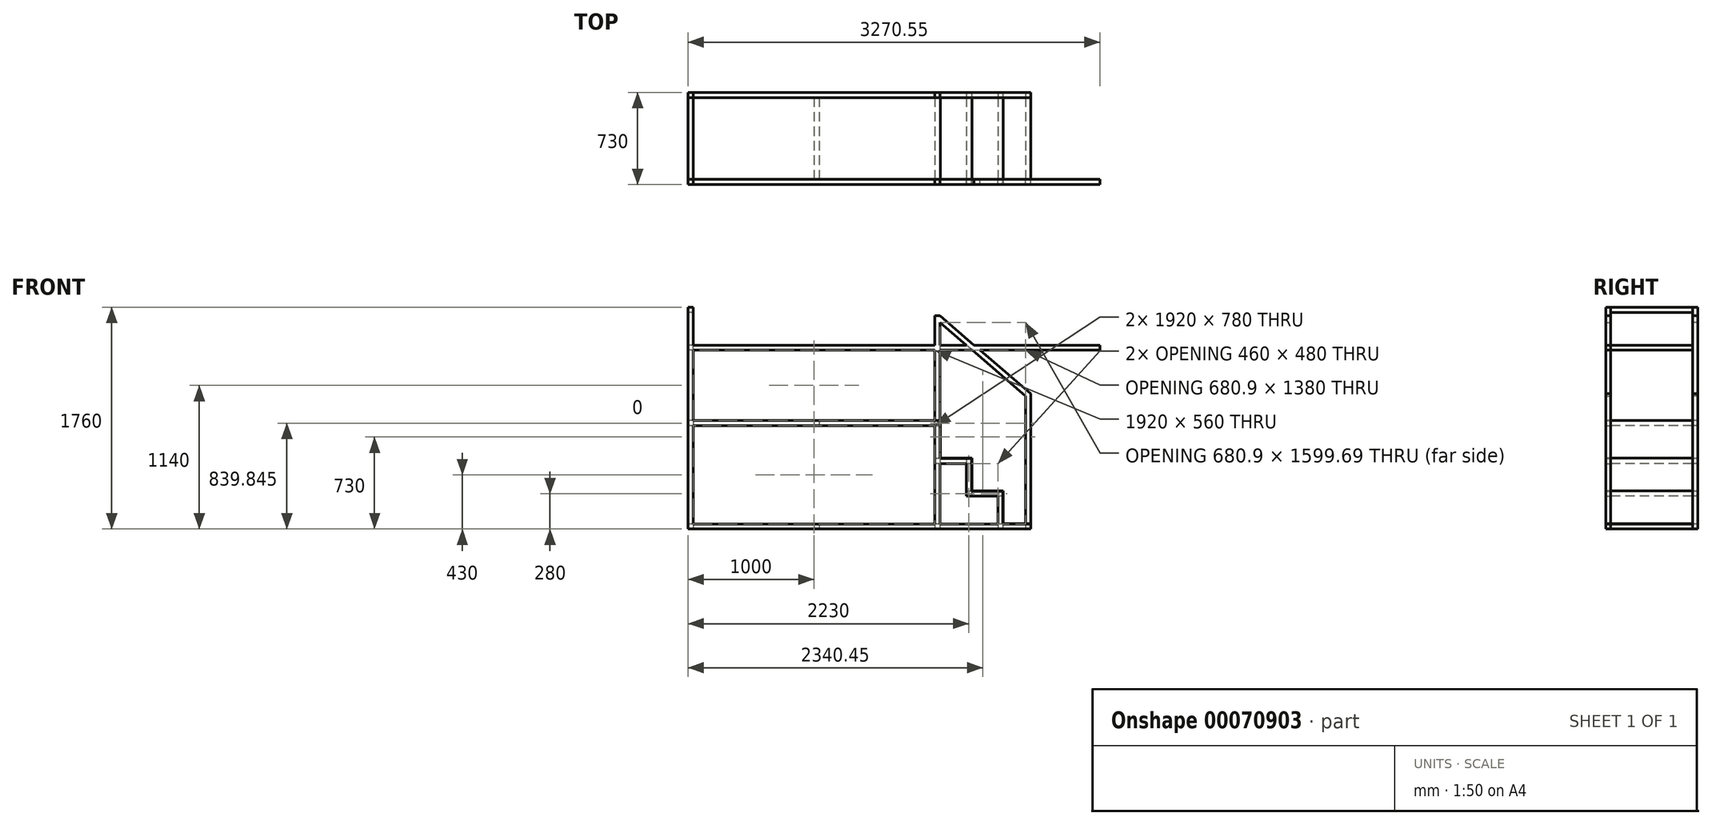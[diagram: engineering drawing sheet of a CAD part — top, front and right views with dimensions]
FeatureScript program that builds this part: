
annotation { "Feature Type Name" : "Feature", "Feature Type Description" : "" }
export const myFeature = defineFeature(function(context is Context, id is Id, definition is map)
    precondition{}
    {
        {
            var Q0;
            Q0=qCreatedBy(makeId("Front.planeOp"),FACE);
            var sketch = newSketch(context, id + "F0", { "sketchPlane" : qUnion([Q0])});
            skLineSegment(sketch, "E0", {"start": v(40, 0) * mm, "end": v(1960, 0) * mm});
            skLineSegment(sketch, "E1.0", {"start": v(40, 40) * mm, "end": v(1960, 40) * mm});
            skLineSegment(sketch, "E2", {"start": v(0, 40) * mm, "end": v(0, 0) * mm});
            skLineSegment(sketch, "E3.0", {"start": v(2000, 40) * mm, "end": v(2000, 0) * mm});
            skLineSegment(sketch, "E4", {"start": v(0, 0) * mm, "end": v(0, -820) * mm});
            skLineSegment(sketch, "E5", {"start": v(2000, 0) * mm, "end": v(2000, -260) * mm});
            skLineSegment(sketch, "E6", {"start": v(0, -820) * mm, "end": v(2000, -820) * mm});
            skLineSegment(sketch, "E7.0", {"start": v(40, -780) * mm, "end": v(1960, -780) * mm});
            skLineSegment(sketch, "E8.0", {"start": v(40, 0) * mm, "end": v(40, -780) * mm});
            skLineSegment(sketch, "E9.0", {"start": v(1960, 0) * mm, "end": v(1960, -780) * mm});
            skLineSegment(sketch, "E10", {"start": v(0, 40) * mm, "end": v(0, 940) * mm});
            skLineSegment(sketch, "E11", {"start": v(0, 940) * mm, "end": v(2000, 940) * mm});
            skLineSegment(sketch, "E12", {"start": v(2000, 940) * mm, "end": v(2000, 872.37) * mm});
            skLineSegment(sketch, "E13", {"start": v(40, 40) * mm, "end": v(40, 900) * mm});
            skLineSegment(sketch, "E14", {"start": v(40, 900) * mm, "end": v(1960, 900) * mm});
            skLineSegment(sketch, "E15", {"start": v(1960, 900) * mm, "end": v(1960, 40) * mm});
            skLineSegment(sketch, "E16", {"start": v(2000, 872.37) * mm, "end": v(2720.9, 254.57) * mm});
            skLineSegment(sketch, "E17", {"start": v(2720.9, 254.57) * mm, "end": v(2720.9, -820) * mm});
            skLineSegment(sketch, "E18", {"start": v(2720.9, -820) * mm, "end": v(2000, -820) * mm});
            skLineSegment(sketch, "E19", {"start": v(1960, -780) * mm, "end": v(2460, -780) * mm});
            skLineSegment(sketch, "E20", {"start": v(2680.9, -780) * mm, "end": v(2680.9, 236.17) * mm});
            skLineSegment(sketch, "E21", {"start": v(2680.9, 236.17) * mm, "end": v(2000, 819.7) * mm});
            skLineSegment(sketch, "E22", {"start": v(2000, -300) * mm, "end": v(2210, -300) * mm});
            skLineSegment(sketch, "E23", {"start": v(2210, -300) * mm, "end": v(2210, -560) * mm});
            skLineSegment(sketch, "E24", {"start": v(2210, -560) * mm, "end": v(2460, -560) * mm});
            skLineSegment(sketch, "E25", {"start": v(2460, -560) * mm, "end": v(2460, -780) * mm});
            skLineSegment(sketch, "E26", {"start": v(2000, -260) * mm, "end": v(2250, -260) * mm});
            skLineSegment(sketch, "E27", {"start": v(2250, -260) * mm, "end": v(2250, -520) * mm});
            skLineSegment(sketch, "E28", {"start": v(2250, -520) * mm, "end": v(2500, -520) * mm});
            skLineSegment(sketch, "E29", {"start": v(2500, -520) * mm, "end": v(2500, -780) * mm});
            skLineSegment(sketch, "E30.trimOffspring", {"start": v(2000, -300) * mm, "end": v(2000, -820) * mm});
            skLineSegment(sketch, "E31.trimOffspring", {"start": v(2500, -780) * mm, "end": v(2680.9, -780) * mm});
            skLineSegment(sketch, "E32.trimOffspring", {"start": v(2000, 819.7) * mm, "end": v(2000, 40) * mm});
            skSolve(sketch);
        }
        {
            var Q0;
            Q0=makeQuery(id+"F0.imprint","IMPRINT",FACE,{"disambiguationData":[TD([[makeQuery(id+"F0.imprint","IMPRINT",EDGE,{"derivedFrom":sQuery(id+"F0.wireOp",EDGE,"E0")}),1.0]])]});
            extrude(context, id + "F1", {"entities" : qUnion([Q0]), "depth" : 40 * mm});
        }
        {
            var Q0;
            Q0=makeQuery(id+"F1.opExtrude","CAP_FACE",FACE,{"disambiguationData":[OSD([sQuery(id+"F0.wireOp",EDGE,"E0"),sQuery(id+"F0.wireOp",EDGE,"E1.0"),sQuery(id+"F0.wireOp",EDGE,"E2"),sQuery(id+"F0.wireOp",EDGE,"E3.0"),sQuery(id+"F0.wireOp",EDGE,"E4"),sQuery(id+"F0.wireOp",EDGE,"E5"),sQuery(id+"F0.wireOp",EDGE,"E6"),sQuery(id+"F0.wireOp",EDGE,"E7.0"),sQuery(id+"F0.wireOp",EDGE,"E8.0"),sQuery(id+"F0.wireOp",EDGE,"E9.0"),sQuery(id+"F0.wireOp",EDGE,"E10"),sQuery(id+"F0.wireOp",EDGE,"E11"),sQuery(id+"F0.wireOp",EDGE,"E12"),sQuery(id+"F0.wireOp",EDGE,"E13"),sQuery(id+"F0.wireOp",EDGE,"E14"),sQuery(id+"F0.wireOp",EDGE,"E15"),sQuery(id+"F0.wireOp",EDGE,"E16"),sQuery(id+"F0.wireOp",EDGE,"E17"),sQuery(id+"F0.wireOp",EDGE,"E18"),sQuery(id+"F0.wireOp",EDGE,"E19"),sQuery(id+"F0.wireOp",EDGE,"E20"),sQuery(id+"F0.wireOp",EDGE,"E21"),sQuery(id+"F0.wireOp",EDGE,"E22"),sQuery(id+"F0.wireOp",EDGE,"E23"),sQuery(id+"F0.wireOp",EDGE,"E24"),sQuery(id+"F0.wireOp",EDGE,"E25"),sQuery(id+"F0.wireOp",EDGE,"E26"),sQuery(id+"F0.wireOp",EDGE,"E27"),sQuery(id+"F0.wireOp",EDGE,"E28"),sQuery(id+"F0.wireOp",EDGE,"E29"),sQuery(id+"F0.wireOp",EDGE,"E30.trimOffspring"),sQuery(id+"F0.wireOp",EDGE,"E31.trimOffspring"),sQuery(id+"F0.wireOp",EDGE,"E32.trimOffspring")])],"isStart":true});
            var sketch = newSketch(context, id + "F2", { "sketchPlane" : qUnion([Q0])});
            skLineSegment(sketch, "E33.bottom", {"start": v(-1960, 0) * mm, "end": v(-2000, 0) * mm});
            skLineSegment(sketch, "E33.top", {"start": v(-1960, 40) * mm, "end": v(-2000, 40) * mm});
            skLineSegment(sketch, "E33.left", {"start": v(-1960, 0) * mm, "end": v(-1960, 40) * mm});
            skLineSegment(sketch, "E33.right", {"start": v(-2000, 0) * mm, "end": v(-2000, 40) * mm});
            skLineSegment(sketch, "E34.bottom", {"start": v(-2000, -260) * mm, "end": v(-1960, -260) * mm});
            skLineSegment(sketch, "E34.top", {"start": v(-2000, -300) * mm, "end": v(-1960, -300) * mm});
            skLineSegment(sketch, "E34.left", {"start": v(-2000, -260) * mm, "end": v(-2000, -300) * mm});
            skLineSegment(sketch, "E34.right", {"start": v(-1960, -260) * mm, "end": v(-1960, -300) * mm});
            skLineSegment(sketch, "E35.bottom", {"start": v(-2250, -260) * mm, "end": v(-2210, -260) * mm});
            skLineSegment(sketch, "E35.top", {"start": v(-2250, -300) * mm, "end": v(-2210, -300) * mm});
            skLineSegment(sketch, "E35.left", {"start": v(-2250, -260) * mm, "end": v(-2250, -300) * mm});
            skLineSegment(sketch, "E35.right", {"start": v(-2210, -260) * mm, "end": v(-2210, -300) * mm});
            skLineSegment(sketch, "E36.bottom", {"start": v(-2250, -520) * mm, "end": v(-2210, -520) * mm});
            skLineSegment(sketch, "E36.top", {"start": v(-2250, -560) * mm, "end": v(-2210, -560) * mm});
            skLineSegment(sketch, "E36.left", {"start": v(-2250, -520) * mm, "end": v(-2250, -560) * mm});
            skLineSegment(sketch, "E36.right", {"start": v(-2210, -520) * mm, "end": v(-2210, -560) * mm});
            skLineSegment(sketch, "E37.bottom", {"start": v(-2500, -520) * mm, "end": v(-2460, -520) * mm});
            skLineSegment(sketch, "E37.top", {"start": v(-2500, -560) * mm, "end": v(-2460, -560) * mm});
            skLineSegment(sketch, "E37.left", {"start": v(-2500, -520) * mm, "end": v(-2500, -560) * mm});
            skLineSegment(sketch, "E37.right", {"start": v(-2460, -520) * mm, "end": v(-2460, -560) * mm});
            skLineSegment(sketch, "E38.bottom", {"start": v(-2680.9, -780) * mm, "end": v(-2720.9, -780) * mm});
            skLineSegment(sketch, "E38.top", {"start": v(-2680.9, -820) * mm, "end": v(-2720.9, -820) * mm});
            skLineSegment(sketch, "E38.left", {"start": v(-2680.9, -780) * mm, "end": v(-2680.9, -820) * mm});
            skLineSegment(sketch, "E38.right", {"start": v(-2720.9, -780) * mm, "end": v(-2720.9, -820) * mm});
            skLineSegment(sketch, "E39.bottom", {"start": v(-40, 40) * mm, "end": v(0, 40) * mm});
            skLineSegment(sketch, "E39.top", {"start": v(-40, 0) * mm, "end": v(0, 0) * mm});
            skLineSegment(sketch, "E39.left", {"start": v(-40, 40) * mm, "end": v(-40, 0) * mm});
            skLineSegment(sketch, "E39.right", {"start": v(0, 40) * mm, "end": v(0, 0) * mm});
            skLineSegment(sketch, "E40.bottom", {"start": v(-40, -780) * mm, "end": v(0, -780) * mm});
            skLineSegment(sketch, "E40.top", {"start": v(-40, -820) * mm, "end": v(0, -820) * mm});
            skLineSegment(sketch, "E40.left", {"start": v(-40, -780) * mm, "end": v(-40, -820) * mm});
            skLineSegment(sketch, "E40.right", {"start": v(0, -780) * mm, "end": v(0, -820) * mm});
            skLineSegment(sketch, "E41.bottom", {"start": v(-2500, -780) * mm, "end": v(-2460, -780) * mm});
            skLineSegment(sketch, "E41.top", {"start": v(-2500, -820) * mm, "end": v(-2460, -820) * mm});
            skLineSegment(sketch, "E41.left", {"start": v(-2500, -780) * mm, "end": v(-2500, -820) * mm});
            skLineSegment(sketch, "E41.right", {"start": v(-2460, -780) * mm, "end": v(-2460, -820) * mm});
            skLineSegment(sketch, "E42.bottom", {"start": v(-2000, -780) * mm, "end": v(-1960, -780) * mm});
            skLineSegment(sketch, "E42.top", {"start": v(-2000, -820) * mm, "end": v(-1960, -820) * mm});
            skLineSegment(sketch, "E42.left", {"start": v(-2000, -780) * mm, "end": v(-2000, -820) * mm});
            skLineSegment(sketch, "E42.right", {"start": v(-1960, -780) * mm, "end": v(-1960, -820) * mm});
            skLineSegment(sketch, "E43.bottom", {"start": v(-1040, 40) * mm, "end": v(-1000, 40) * mm});
            skLineSegment(sketch, "E43.top", {"start": v(-1040, 0) * mm, "end": v(-1000, 0) * mm});
            skLineSegment(sketch, "E43.left", {"start": v(-1040, 40) * mm, "end": v(-1040, 0) * mm});
            skLineSegment(sketch, "E43.right", {"start": v(-1000, 40) * mm, "end": v(-1000, 0) * mm});
            skLineSegment(sketch, "E44.bottom", {"start": v(-1040, -780) * mm, "end": v(-1000, -780) * mm});
            skLineSegment(sketch, "E44.top", {"start": v(-1040, -820) * mm, "end": v(-1000, -820) * mm});
            skLineSegment(sketch, "E44.left", {"start": v(-1040, -780) * mm, "end": v(-1040, -820) * mm});
            skLineSegment(sketch, "E44.right", {"start": v(-1000, -780) * mm, "end": v(-1000, -820) * mm});
            skLineSegment(sketch, "E45.bottom", {"start": v(-40, 900) * mm, "end": v(0, 900) * mm});
            skLineSegment(sketch, "E45.top", {"start": v(-40, 940) * mm, "end": v(0, 940) * mm});
            skLineSegment(sketch, "E45.left", {"start": v(-40, 900) * mm, "end": v(-40, 940) * mm});
            skLineSegment(sketch, "E45.right", {"start": v(0, 900) * mm, "end": v(0, 940) * mm});
            skSolve(sketch);
        }
        {
            var Q0;
            Q0=makeQuery(id+"F2.imprint","IMPRINT",FACE,{"disambiguationData":[TD([[makeQuery(id+"F2.imprint","IMPRINT",EDGE,{"derivedFrom":sQuery(id+"F2.wireOp",EDGE,"E45.bottom")}),1.0]])]});
            var Q1;
            Q1=makeQuery(id+"F2.imprint","IMPRINT",FACE,{"disambiguationData":[TD([[makeQuery(id+"F2.imprint","IMPRINT",EDGE,{"derivedFrom":sQuery(id+"F2.wireOp",EDGE,"E39.bottom")}),-1.0]])]});
            var Q2;
            Q2=makeQuery(id+"F2.imprint","IMPRINT",FACE,{"disambiguationData":[TD([[makeQuery(id+"F2.imprint","IMPRINT",EDGE,{"derivedFrom":sQuery(id+"F2.wireOp",EDGE,"E40.bottom")}),-1.0]])]});
            var Q3;
            Q3=makeQuery(id+"F2.imprint","IMPRINT",FACE,{"disambiguationData":[TD([[makeQuery(id+"F2.imprint","IMPRINT",EDGE,{"derivedFrom":sQuery(id+"F2.wireOp",EDGE,"E44.bottom")}),1.0]])]});
            var Q4;
            Q4=makeQuery(id+"F2.imprint","IMPRINT",FACE,{"disambiguationData":[TD([[makeQuery(id+"F2.imprint","IMPRINT",EDGE,{"derivedFrom":sQuery(id+"F2.wireOp",EDGE,"E43.bottom")}),1.0]])]});
            var Q5;
            Q5=makeQuery(id+"F2.imprint","IMPRINT",FACE,{"disambiguationData":[TD([[makeQuery(id+"F2.imprint","IMPRINT",EDGE,{"derivedFrom":sQuery(id+"F2.wireOp",EDGE,"E33.bottom")}),-1.0]])]});
            var Q6;
            Q6=makeQuery(id+"F2.imprint","IMPRINT",FACE,{"disambiguationData":[TD([[makeQuery(id+"F2.imprint","IMPRINT",EDGE,{"derivedFrom":sQuery(id+"F2.wireOp",EDGE,"E42.bottom")}),-1.0]])]});
            var Q7;
            Q7=makeQuery(id+"F2.imprint","IMPRINT",FACE,{"disambiguationData":[TD([[makeQuery(id+"F2.imprint","IMPRINT",EDGE,{"derivedFrom":sQuery(id+"F2.wireOp",EDGE,"E34.bottom")}),-1.0]])]});
            var Q8;
            Q8=makeQuery(id+"F2.imprint","IMPRINT",FACE,{"disambiguationData":[TD([[makeQuery(id+"F2.imprint","IMPRINT",EDGE,{"derivedFrom":sQuery(id+"F2.wireOp",EDGE,"E35.bottom")}),1.0]])]});
            var Q9;
            Q9=makeQuery(id+"F2.imprint","IMPRINT",FACE,{"disambiguationData":[TD([[makeQuery(id+"F2.imprint","IMPRINT",EDGE,{"derivedFrom":sQuery(id+"F2.wireOp",EDGE,"E37.bottom")}),1.0]])]});
            var Q10;
            Q10=makeQuery(id+"F2.imprint","IMPRINT",FACE,{"disambiguationData":[TD([[makeQuery(id+"F2.imprint","IMPRINT",EDGE,{"derivedFrom":sQuery(id+"F2.wireOp",EDGE,"E36.bottom")}),-1.0]])]});
            var Q11;
            Q11=makeQuery(id+"F2.imprint","IMPRINT",FACE,{"disambiguationData":[TD([[makeQuery(id+"F2.imprint","IMPRINT",EDGE,{"derivedFrom":sQuery(id+"F2.wireOp",EDGE,"E41.bottom")}),-1.0]])]});
            var Q12;
            Q12=makeQuery(id+"F2.imprint","IMPRINT",FACE,{"disambiguationData":[TD([[makeQuery(id+"F2.imprint","IMPRINT",EDGE,{"derivedFrom":sQuery(id+"F2.wireOp",EDGE,"E38.bottom")}),1.0]])]});
            extrude(context, id + "F3", {"entities" : qUnion([Q0, Q1, Q2, Q3, Q4, Q5, Q6, Q7, Q8, Q9, Q10, Q11, Q12]), "depth" : 650 * mm});
        }
        {
            var Q0;
            Q0=makeQuery(id+"F1.opExtrude","CAP_FACE",FACE,{"disambiguationData":[OSD([sQuery(id+"F0.wireOp",EDGE,"E0"),sQuery(id+"F0.wireOp",EDGE,"E1.0"),sQuery(id+"F0.wireOp",EDGE,"E2"),sQuery(id+"F0.wireOp",EDGE,"E3.0"),sQuery(id+"F0.wireOp",EDGE,"E4"),sQuery(id+"F0.wireOp",EDGE,"E5"),sQuery(id+"F0.wireOp",EDGE,"E6"),sQuery(id+"F0.wireOp",EDGE,"E7.0"),sQuery(id+"F0.wireOp",EDGE,"E8.0"),sQuery(id+"F0.wireOp",EDGE,"E9.0"),sQuery(id+"F0.wireOp",EDGE,"E10"),sQuery(id+"F0.wireOp",EDGE,"E11"),sQuery(id+"F0.wireOp",EDGE,"E12"),sQuery(id+"F0.wireOp",EDGE,"E13"),sQuery(id+"F0.wireOp",EDGE,"E14"),sQuery(id+"F0.wireOp",EDGE,"E15"),sQuery(id+"F0.wireOp",EDGE,"E16"),sQuery(id+"F0.wireOp",EDGE,"E17"),sQuery(id+"F0.wireOp",EDGE,"E18"),sQuery(id+"F0.wireOp",EDGE,"E19"),sQuery(id+"F0.wireOp",EDGE,"E20"),sQuery(id+"F0.wireOp",EDGE,"E21"),sQuery(id+"F0.wireOp",EDGE,"E22"),sQuery(id+"F0.wireOp",EDGE,"E23"),sQuery(id+"F0.wireOp",EDGE,"E24"),sQuery(id+"F0.wireOp",EDGE,"E25"),sQuery(id+"F0.wireOp",EDGE,"E26"),sQuery(id+"F0.wireOp",EDGE,"E27"),sQuery(id+"F0.wireOp",EDGE,"E28"),sQuery(id+"F0.wireOp",EDGE,"E29"),sQuery(id+"F0.wireOp",EDGE,"E30.trimOffspring"),sQuery(id+"F0.wireOp",EDGE,"E31.trimOffspring"),sQuery(id+"F0.wireOp",EDGE,"E32.trimOffspring")])],"isStart":true});
            cPlane(context, id + "F4", {"entities" : qUnion([Q0]), "cplaneType" : CPlaneType.OFFSET, "offset" : 325 * mm, "width" : 150 * mm, "height" : 150 * mm});
        }
        {
            var Q0;
            Q0=makeQuery(id+"F1.opExtrude","SWEPT_BODY",BODY,{"disambiguationData":[OSD([sQuery(id+"F0.wireOp",EDGE,"E0"),sQuery(id+"F0.wireOp",EDGE,"E1.0"),sQuery(id+"F0.wireOp",EDGE,"E2"),sQuery(id+"F0.wireOp",EDGE,"E3.0"),sQuery(id+"F0.wireOp",EDGE,"E4"),sQuery(id+"F0.wireOp",EDGE,"E5"),sQuery(id+"F0.wireOp",EDGE,"E6"),sQuery(id+"F0.wireOp",EDGE,"E7.0"),sQuery(id+"F0.wireOp",EDGE,"E8.0"),sQuery(id+"F0.wireOp",EDGE,"E9.0"),sQuery(id+"F0.wireOp",EDGE,"E10"),sQuery(id+"F0.wireOp",EDGE,"E11"),sQuery(id+"F0.wireOp",EDGE,"E12"),sQuery(id+"F0.wireOp",EDGE,"E13"),sQuery(id+"F0.wireOp",EDGE,"E14"),sQuery(id+"F0.wireOp",EDGE,"E15"),sQuery(id+"F0.wireOp",EDGE,"E16"),sQuery(id+"F0.wireOp",EDGE,"E17"),sQuery(id+"F0.wireOp",EDGE,"E18"),sQuery(id+"F0.wireOp",EDGE,"E19"),sQuery(id+"F0.wireOp",EDGE,"E20"),sQuery(id+"F0.wireOp",EDGE,"E21"),sQuery(id+"F0.wireOp",EDGE,"E22"),sQuery(id+"F0.wireOp",EDGE,"E23"),sQuery(id+"F0.wireOp",EDGE,"E24"),sQuery(id+"F0.wireOp",EDGE,"E25"),sQuery(id+"F0.wireOp",EDGE,"E26"),sQuery(id+"F0.wireOp",EDGE,"E27"),sQuery(id+"F0.wireOp",EDGE,"E28"),sQuery(id+"F0.wireOp",EDGE,"E29"),sQuery(id+"F0.wireOp",EDGE,"E30.trimOffspring"),sQuery(id+"F0.wireOp",EDGE,"E31.trimOffspring"),sQuery(id+"F0.wireOp",EDGE,"E32.trimOffspring")])]});
            var Q1;
            Q1=qCreatedBy(id+"F4.planeOp",FACE);
            mirror(context, id + "F5", {"entities" : qUnion([Q0]), "mirrorPlane" : qUnion([Q1])});
        }
        {
            var Q0;
            Q0=makeQuery(id+"F1.opExtrude","CAP_FACE",FACE,{"disambiguationData":[OSD([sQuery(id+"F0.wireOp",EDGE,"E0"),sQuery(id+"F0.wireOp",EDGE,"E1.0"),sQuery(id+"F0.wireOp",EDGE,"E2"),sQuery(id+"F0.wireOp",EDGE,"E3.0"),sQuery(id+"F0.wireOp",EDGE,"E4"),sQuery(id+"F0.wireOp",EDGE,"E5"),sQuery(id+"F0.wireOp",EDGE,"E6"),sQuery(id+"F0.wireOp",EDGE,"E7.0"),sQuery(id+"F0.wireOp",EDGE,"E8.0"),sQuery(id+"F0.wireOp",EDGE,"E9.0"),sQuery(id+"F0.wireOp",EDGE,"E10"),sQuery(id+"F0.wireOp",EDGE,"E11"),sQuery(id+"F0.wireOp",EDGE,"E12"),sQuery(id+"F0.wireOp",EDGE,"E13"),sQuery(id+"F0.wireOp",EDGE,"E14"),sQuery(id+"F0.wireOp",EDGE,"E15"),sQuery(id+"F0.wireOp",EDGE,"E16"),sQuery(id+"F0.wireOp",EDGE,"E17"),sQuery(id+"F0.wireOp",EDGE,"E18"),sQuery(id+"F0.wireOp",EDGE,"E19"),sQuery(id+"F0.wireOp",EDGE,"E20"),sQuery(id+"F0.wireOp",EDGE,"E21"),sQuery(id+"F0.wireOp",EDGE,"E22"),sQuery(id+"F0.wireOp",EDGE,"E23"),sQuery(id+"F0.wireOp",EDGE,"E24"),sQuery(id+"F0.wireOp",EDGE,"E25"),sQuery(id+"F0.wireOp",EDGE,"E26"),sQuery(id+"F0.wireOp",EDGE,"E27"),sQuery(id+"F0.wireOp",EDGE,"E28"),sQuery(id+"F0.wireOp",EDGE,"E29"),sQuery(id+"F0.wireOp",EDGE,"E30.trimOffspring"),sQuery(id+"F0.wireOp",EDGE,"E31.trimOffspring"),sQuery(id+"F0.wireOp",EDGE,"E32.trimOffspring")])],"isStart":false});
            var sketch = newSketch(context, id + "F6", { "sketchPlane" : qUnion([Q0])});
            skLineSegment(sketch, "E46", {"start": v(40, 40) * mm, "end": v(2000, 40) * mm});
            skLineSegment(sketch, "E47", {"start": v(2000, 40) * mm, "end": v(2000, -260) * mm});
            skLineSegment(sketch, "E48", {"start": v(2000, -260) * mm, "end": v(2250, -260) * mm});
            skLineSegment(sketch, "E49", {"start": v(2250, -260) * mm, "end": v(2250, -520) * mm});
            skLineSegment(sketch, "E50", {"start": v(2250, -520) * mm, "end": v(2500, -520) * mm});
            skLineSegment(sketch, "E51", {"start": v(2500, -520) * mm, "end": v(2500, -780) * mm});
            skLineSegment(sketch, "E52", {"start": v(2500, -780) * mm, "end": v(2720.9, -780) * mm});
            skLineSegment(sketch, "E53.0", {"start": v(2503, -777) * mm, "end": v(2720.9, -777) * mm});
            skLineSegment(sketch, "E53.1", {"start": v(2503, -517) * mm, "end": v(2503, -777) * mm});
            skLineSegment(sketch, "E53.2", {"start": v(2253, -517) * mm, "end": v(2503, -517) * mm});
            skLineSegment(sketch, "E53.3", {"start": v(40, 43) * mm, "end": v(2003, 43) * mm});
            skLineSegment(sketch, "E53.4", {"start": v(2003, 43) * mm, "end": v(2003, -257) * mm});
            skLineSegment(sketch, "E53.5", {"start": v(2003, -257) * mm, "end": v(2253, -257) * mm});
            skLineSegment(sketch, "E53.6", {"start": v(2253, -257) * mm, "end": v(2253, -517) * mm});
            skLineSegment(sketch, "E54", {"start": v(2720.9, -777) * mm, "end": v(2720.9, -780) * mm});
            skLineSegment(sketch, "E55", {"start": v(40, 43) * mm, "end": v(40, 40) * mm});
            skSolve(sketch);
        }
        {
            var Q0;
            {var subQ0=sQuery(id+"F6.wireOp",EDGE,"E55");Q0=makeQuery(id+"F6.imprint","IMPRINT",FACE,{"disambiguationData":[TD([[makeQuery(id+"F6.imprint","IMPRINT",EDGE,{"derivedFrom":subQ0}),-1.0]])]});}
            var Q1;
            {var subQ0=sQuery(id+"F6.wireOp",EDGE,"E46");var subQ1=makeQuery(id+"F1.opExtrude","CAP_EDGE",EDGE,{"disambiguationData":[OSD([sQuery(id+"F0.wireOp",EDGE,"E15")])],"isStart":false});var subQ2=makeQuery(id+"F6.imprint","INTERSECT",VERTEX,{"derivedFrom":[subQ1,subQ0]});Q1=makeQuery(id+"F6.imprint","IMPRINT",FACE,{"disambiguationData":[TD([[makeQuery(id+"F6.imprint","IMPRINT",EDGE,{"disambiguationData":[TD([[subQ2,1.0]])],"derivedFrom":subQ1}),1.0]])]});}
            var Q2;
            {var subQ11=sQuery(id+"F6.wireOp",EDGE,"E47");Q2=makeQuery(id+"F6.imprint","IMPRINT",FACE,{"disambiguationData":[TD([[makeQuery(id+"F6.imprint","IMPRINT",EDGE,{"derivedFrom":subQ11}),1.0]])]});}
            var Q3;
            {var subQ3=sQuery(id+"F6.wireOp",EDGE,"E54");Q3=makeQuery(id+"F6.imprint","IMPRINT",FACE,{"disambiguationData":[TD([[makeQuery(id+"F6.imprint","IMPRINT",EDGE,{"derivedFrom":subQ3}),-1.0]])]});}
            extrude(context, id + "F7", {"entities" : qUnion([Q0, Q1, Q2, Q3]), "oppositeDirection" : true, "depth" : 690 * mm});
        }
        {
            var Q0;
            Q0=makeQuery(id+"F5.opPattern","COPY",FACE,{"derivedFrom":makeQuery(id+"F1.opExtrude","CAP_FACE",FACE,{"disambiguationData":[OSD([sQuery(id+"F0.wireOp",EDGE,"E0"),sQuery(id+"F0.wireOp",EDGE,"E1.0"),sQuery(id+"F0.wireOp",EDGE,"E2"),sQuery(id+"F0.wireOp",EDGE,"E3.0"),sQuery(id+"F0.wireOp",EDGE,"E4"),sQuery(id+"F0.wireOp",EDGE,"E5"),sQuery(id+"F0.wireOp",EDGE,"E6"),sQuery(id+"F0.wireOp",EDGE,"E7.0"),sQuery(id+"F0.wireOp",EDGE,"E8.0"),sQuery(id+"F0.wireOp",EDGE,"E9.0"),sQuery(id+"F0.wireOp",EDGE,"E10"),sQuery(id+"F0.wireOp",EDGE,"E11"),sQuery(id+"F0.wireOp",EDGE,"E12"),sQuery(id+"F0.wireOp",EDGE,"E13"),sQuery(id+"F0.wireOp",EDGE,"E14"),sQuery(id+"F0.wireOp",EDGE,"E15"),sQuery(id+"F0.wireOp",EDGE,"E16"),sQuery(id+"F0.wireOp",EDGE,"E17"),sQuery(id+"F0.wireOp",EDGE,"E18"),sQuery(id+"F0.wireOp",EDGE,"E19"),sQuery(id+"F0.wireOp",EDGE,"E20"),sQuery(id+"F0.wireOp",EDGE,"E21"),sQuery(id+"F0.wireOp",EDGE,"E22"),sQuery(id+"F0.wireOp",EDGE,"E23"),sQuery(id+"F0.wireOp",EDGE,"E24"),sQuery(id+"F0.wireOp",EDGE,"E25"),sQuery(id+"F0.wireOp",EDGE,"E26"),sQuery(id+"F0.wireOp",EDGE,"E27"),sQuery(id+"F0.wireOp",EDGE,"E28"),sQuery(id+"F0.wireOp",EDGE,"E29"),sQuery(id+"F0.wireOp",EDGE,"E30.trimOffspring"),sQuery(id+"F0.wireOp",EDGE,"E31.trimOffspring"),sQuery(id+"F0.wireOp",EDGE,"E32.trimOffspring")])],"isStart":false}),"instanceName":"1"});
            var sketch = newSketch(context, id + "F8", { "sketchPlane" : qUnion([Q0])});
            skLineSegment(sketch, "E56.bottom", {"start": v(-2000, 940) * mm, "end": v(0, 940) * mm});
            skLineSegment(sketch, "E56.left", {"start": v(-2000, 940) * mm, "end": v(-2000, 940) * mm});
            skLineSegment(sketch, "E56.right", {"start": v(-40, 940) * mm, "end": v(-40, 872.37) * mm});
            skLineSegment(sketch, "E57", {"start": v(-2000, 940) * mm, "end": v(-2000, 872.37) * mm});
            skLineSegment(sketch, "E58", {"start": v(-2000, 872.37) * mm, "end": v(-40, 872.37) * mm});
            skSolve(sketch);
        }
        {
            var Q0;
            Q0=makeQuery(id+"F8.imprint","IMPRINT",FACE,{"disambiguationData":[TD([[makeQuery(id+"F8.imprint","IMPRINT",EDGE,{"derivedFrom":sQuery(id+"F8.wireOp",EDGE,"E56.bottom")}),1.0]])]});
            var Q1;
            {var subQ2=sQuery(id+"F8.wireOp",EDGE,"E57");Q1=makeQuery(id+"F8.imprint","IMPRINT",FACE,{"disambiguationData":[TD([[makeQuery(id+"F8.imprint","IMPRINT",EDGE,{"derivedFrom":subQ2}),1.0]])]});}
            extrude(context, id + "F9", {"entities" : qUnion([Q0, Q1]), "operationType" : NewBodyOperationType.REMOVE, "oppositeDirection" : true, "depth" : 760 * mm});
        }
        {
            var Q0;
            Q0=makeQuery(id+"F1.opExtrude","CAP_FACE",FACE,{"disambiguationData":[OSD([sQuery(id+"F0.wireOp",EDGE,"E0"),sQuery(id+"F0.wireOp",EDGE,"E1.0"),sQuery(id+"F0.wireOp",EDGE,"E2"),sQuery(id+"F0.wireOp",EDGE,"E3.0"),sQuery(id+"F0.wireOp",EDGE,"E4"),sQuery(id+"F0.wireOp",EDGE,"E5"),sQuery(id+"F0.wireOp",EDGE,"E6"),sQuery(id+"F0.wireOp",EDGE,"E7.0"),sQuery(id+"F0.wireOp",EDGE,"E8.0"),sQuery(id+"F0.wireOp",EDGE,"E9.0"),sQuery(id+"F0.wireOp",EDGE,"E10"),sQuery(id+"F0.wireOp",EDGE,"E11"),sQuery(id+"F0.wireOp",EDGE,"E12"),sQuery(id+"F0.wireOp",EDGE,"E13"),sQuery(id+"F0.wireOp",EDGE,"E14"),sQuery(id+"F0.wireOp",EDGE,"E15"),sQuery(id+"F0.wireOp",EDGE,"E16"),sQuery(id+"F0.wireOp",EDGE,"E17"),sQuery(id+"F0.wireOp",EDGE,"E18"),sQuery(id+"F0.wireOp",EDGE,"E19"),sQuery(id+"F0.wireOp",EDGE,"E20"),sQuery(id+"F0.wireOp",EDGE,"E21"),sQuery(id+"F0.wireOp",EDGE,"E22"),sQuery(id+"F0.wireOp",EDGE,"E23"),sQuery(id+"F0.wireOp",EDGE,"E24"),sQuery(id+"F0.wireOp",EDGE,"E25"),sQuery(id+"F0.wireOp",EDGE,"E26"),sQuery(id+"F0.wireOp",EDGE,"E27"),sQuery(id+"F0.wireOp",EDGE,"E28"),sQuery(id+"F0.wireOp",EDGE,"E29"),sQuery(id+"F0.wireOp",EDGE,"E30.trimOffspring"),sQuery(id+"F0.wireOp",EDGE,"E31.trimOffspring"),sQuery(id+"F0.wireOp",EDGE,"E32.trimOffspring")])],"isStart":false});
            var sketch = newSketch(context, id + "F10", { "sketchPlane" : qUnion([Q0])});
            skLineSegment(sketch, "E59", {"start": v(0, 640) * mm, "end": v(3270.55, 640) * mm});
            skLineSegment(sketch, "E60.0", {"start": v(0, 600) * mm, "end": v(3270.55, 600) * mm});
            skLineSegment(sketch, "E61", {"start": v(3270.55, 640) * mm, "end": v(3270.55, 600) * mm});
            skSolve(sketch);
        }
        {
            var Q0;
            {var subQ0=sQuery(id+"F10.wireOp",EDGE,"E59");var subQ1=makeQuery(id+"F1.opExtrude","CAP_EDGE",EDGE,{"disambiguationData":[OSD([sQuery(id+"F0.wireOp",EDGE,"E13")])],"isStart":false});var subQ2=makeQuery(id+"F10.imprint","INTERSECT",VERTEX,{"derivedFrom":[subQ1,subQ0]});Q0=makeQuery(id+"F10.imprint","IMPRINT",FACE,{"disambiguationData":[TD([[makeQuery(id+"F10.imprint","IMPRINT",EDGE,{"disambiguationData":[TD([[subQ2,-1.0]])],"derivedFrom":subQ0}),-1.0]])]});}
            extrude(context, id + "F11", {"entities" : qUnion([Q0]), "operationType" : NewBodyOperationType.ADD, "oppositeDirection" : true, "depth" : 40 * mm});
        }
        {
            var Q0;
            Q0=makeQuery(id+"F1.opExtrude","SWEPT_FACE",FACE,{"disambiguationData":[OSD([sQuery(id+"F0.wireOp",EDGE,"E2"),sQuery(id+"F0.wireOp",EDGE,"E4"),sQuery(id+"F0.wireOp",EDGE,"E10")])]});
            var sketch = newSketch(context, id + "F12", { "sketchPlane" : qUnion([Q0])});
            skLineSegment(sketch, "E62", {"start": v(0, 640) * mm, "end": v(-664.21, 640) * mm});
            skLineSegment(sketch, "E63", {"start": v(-664.21, 640) * mm, "end": v(-664.21, 600) * mm});
            skLineSegment(sketch, "E64", {"start": v(-664.21, 600) * mm, "end": v(0, 600) * mm});
            skLineSegment(sketch, "E65", {"start": v(0, 640) * mm, "end": v(0, 600) * mm});
            skSolve(sketch);
        }
        {
            var Q0;
            Q0=makeQuery(id+"F12.imprint","IMPRINT",FACE,{"disambiguationData":[TD([[makeQuery(id+"F12.imprint","IMPRINT",EDGE,{"derivedFrom":sQuery(id+"F12.wireOp",EDGE,"E62")}),1.0]])]});
            extrude(context, id + "F13", {"entities" : qUnion([Q0]), "operationType" : NewBodyOperationType.ADD, "oppositeDirection" : true, "depth" : 40 * mm});
        }
    });
